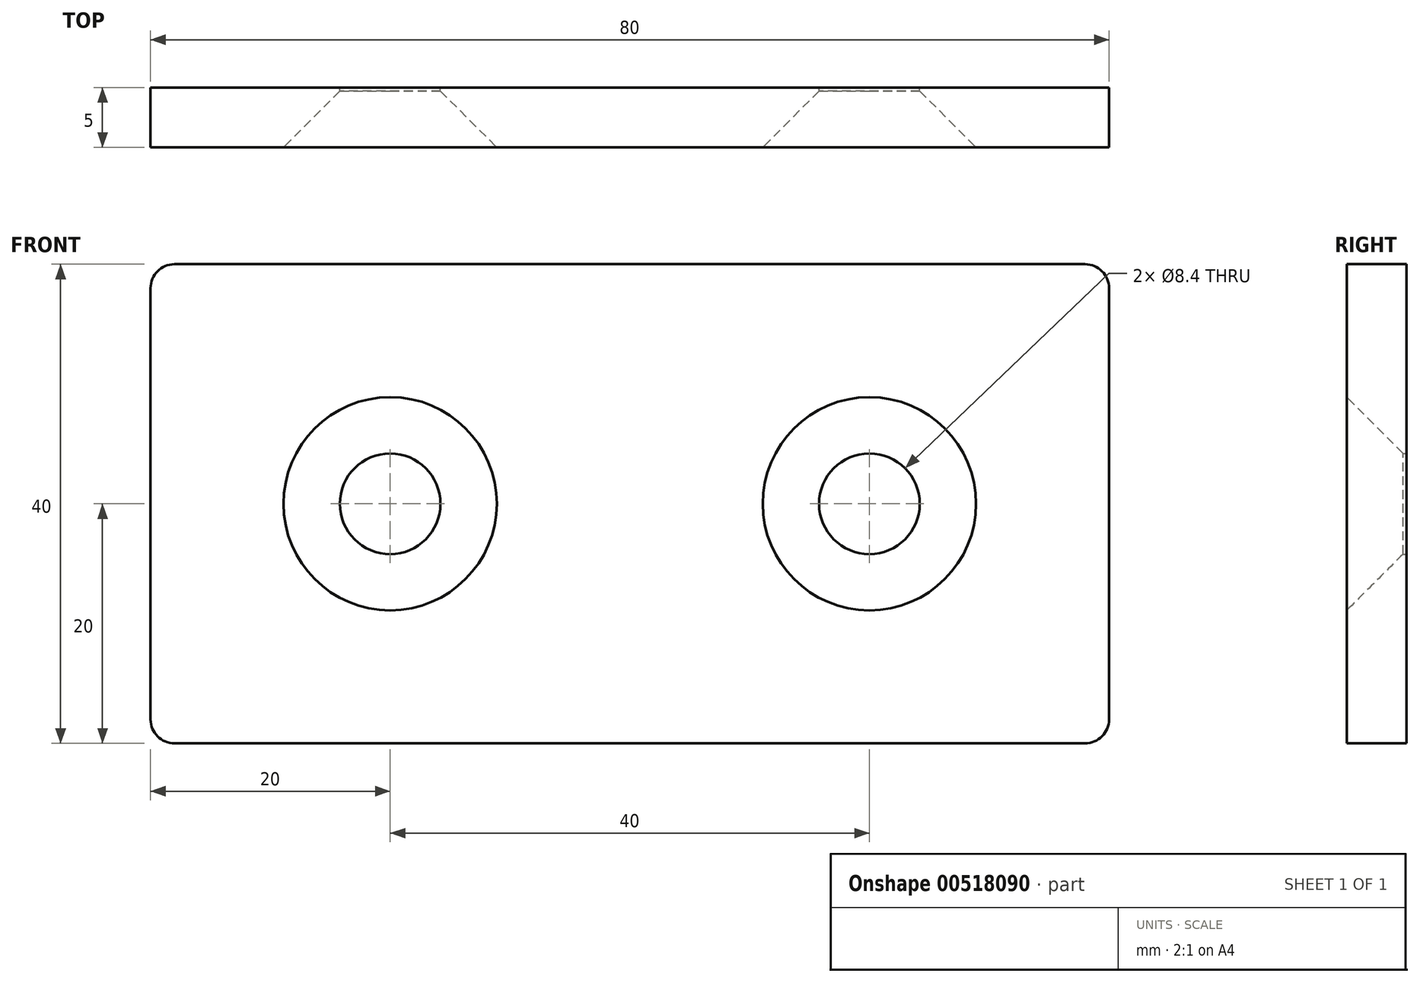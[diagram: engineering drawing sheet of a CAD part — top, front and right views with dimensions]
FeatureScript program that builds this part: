
annotation { "Feature Type Name" : "Feature", "Feature Type Description" : "" }
export const myFeature = defineFeature(function(context is Context, id is Id, definition is map)
    precondition{}
    {
        {
            var Q0;
            Q0=qCreatedBy(makeId("Front.planeOp"),FACE);
            var sketch = newSketch(context, id + "F0", { "sketchPlane" : qUnion([Q0])});
            skCircle(sketch, "E0", {"center": v(0, 0) * mm, "radius": 4.2 * mm});
            skCircle(sketch, "E1.1.0.0", {"center": v(40, 0) * mm, "radius": 4.2 * mm});
            skLineSegment(sketch, "E1.direction1", {"start": v(0, 0) * mm, "end": v(40, 0) * mm, "construction": true});
            skLineSegment(sketch, "E2.bottom", {"start": v(-18, 20) * mm, "end": v(58, 20) * mm});
            skLineSegment(sketch, "E2.top", {"start": v(-18, -20) * mm, "end": v(58, -20) * mm});
            skLineSegment(sketch, "E2.left", {"start": v(-20, 18) * mm, "end": v(-20, -18) * mm});
            skLineSegment(sketch, "E2.right", {"start": v(60, 18) * mm, "end": v(60, -18) * mm});
            skLineSegment(sketch, "E3", {"start": v(0, 0) * mm, "end": v(-20, 0) * mm, "construction": true});
            skLineSegment(sketch, "E4", {"start": v(40, 0) * mm, "end": v(60, 0) * mm, "construction": true});
            skPoint(sketch, "E5.visualSharp", {"position": v(-20, 20) * mm});
            skArc(sketch, "E5.filletArc", {"start": v(-18, 20) * mm, "mid": v(-19.41, 19.41) * mm, "end": v(-20, 18) * mm});
            skPoint(sketch, "E6.visualSharp", {"position": v(-20, -20) * mm});
            skArc(sketch, "E6.filletArc", {"start": v(-20, -18) * mm, "mid": v(-19.41, -19.41) * mm, "end": v(-18, -20) * mm});
            skPoint(sketch, "E7.visualSharp", {"position": v(60, -20) * mm});
            skArc(sketch, "E7.filletArc", {"start": v(58, -20) * mm, "mid": v(59.41, -19.41) * mm, "end": v(60, -18) * mm});
            skPoint(sketch, "E8.visualSharp", {"position": v(60, 20) * mm});
            skArc(sketch, "E8.filletArc", {"start": v(60, 18) * mm, "mid": v(59.41, 19.41) * mm, "end": v(58, 20) * mm});
            skSolve(sketch);
        }
        {
            var Q0;
            Q0=makeQuery(id+"F0.imprint","IMPRINT",FACE,{"disambiguationData":[TD([[makeQuery(id+"F0.imprint","IMPRINT",EDGE,{"derivedFrom":sQuery(id+"F0.wireOp",EDGE,"E0")}),-1.0]])]});
            extrude(context, id + "F1", {"entities" : qUnion([Q0]), "depth" : 5 * mm, "offsetDistance" : 25 * mm});
        }
        {
            var Q0;
            Q0=makeQuery(id+"F1.opExtrude","CAP_EDGE",EDGE,{"disambiguationData":[OSD([sQuery(id+"F0.wireOp",EDGE,"E0")])],"isStart":false});
            var Q1;
            Q1=makeQuery(id+"F1.opExtrude","CAP_EDGE",EDGE,{"disambiguationData":[OSD([sQuery(id+"F0.wireOp",EDGE,"E1.1.0.0")])],"isStart":false});
            var Q2;
            Q2=makeQuery(id+"F1.opExtrude","CAP_EDGE",EDGE,{"disambiguationData":[OSD([sQuery(id+"F0.wireOp",EDGE,"E1.2.0.0")])],"isStart":false});
            var Q3;
            Q3=makeQuery(id+"F1.opExtrude","CAP_EDGE",EDGE,{"disambiguationData":[OSD([sQuery(id+"F0.wireOp",EDGE,"E1.3.0.0")])],"isStart":false});
            chamfer(context, id + "F2", {"entities" : qUnion([Q0, Q1, Q2, Q3]), "width" : 4.7 * mm, "tangentPropagation" : true});
        }
    });
